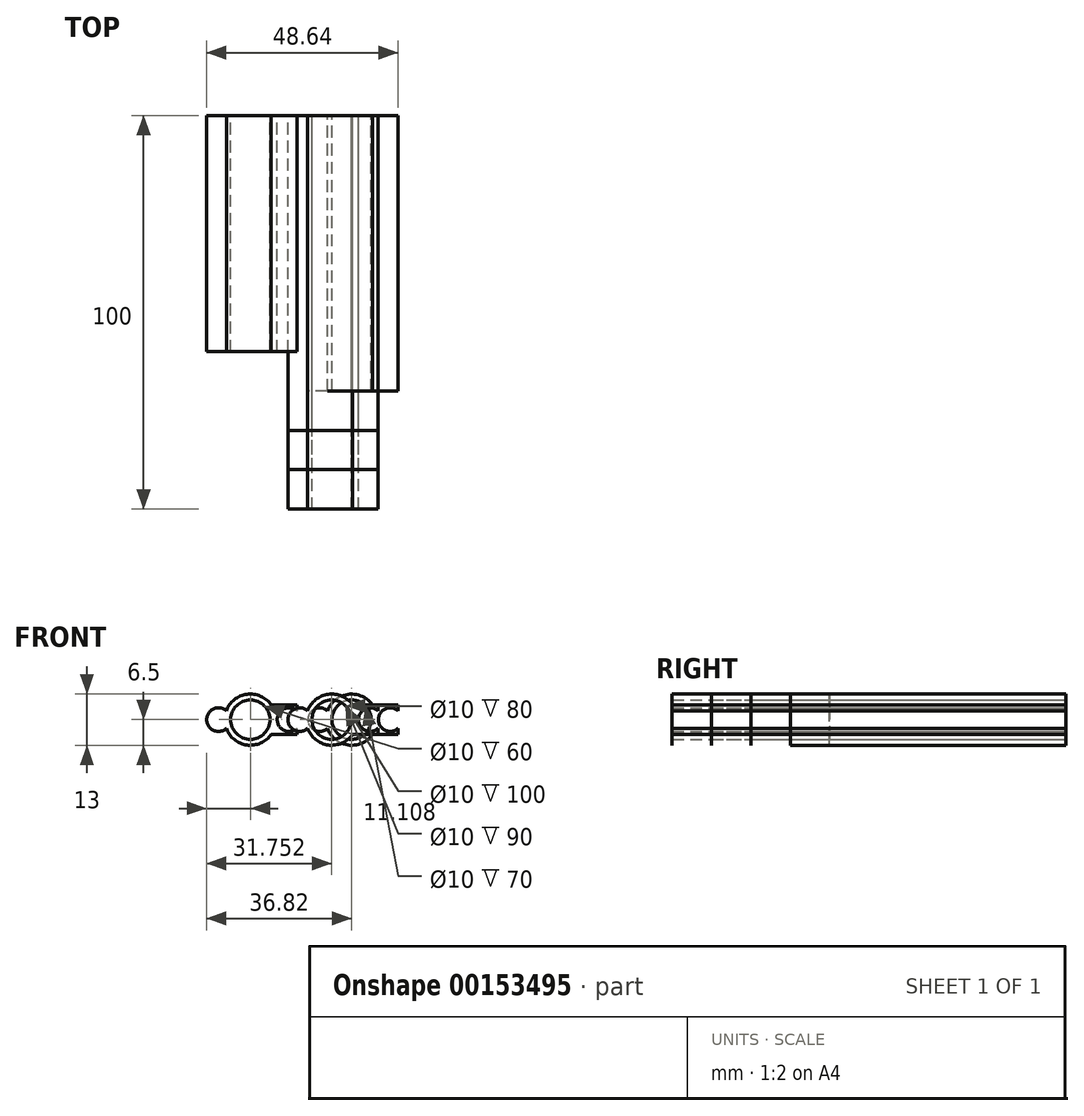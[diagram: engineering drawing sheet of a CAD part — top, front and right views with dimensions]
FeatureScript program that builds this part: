
annotation { "Feature Type Name" : "Feature", "Feature Type Description" : "" }
export const myFeature = defineFeature(function(context is Context, id is Id, definition is map)
    precondition{}
    {
        {
            var Q0;
            Q0=qCreatedBy(makeId("Front.planeOp"),FACE);
            var sketch = newSketch(context, id + "F0", { "sketchPlane" : qUnion([Q0])});
            skCircle(sketch, "E0", {"center": v(0, 0) * mm, "radius": 6.5 * mm});
            skArc(sketch, "E1", {"start": v(-6.1, 2.24) * mm, "mid": v(-11.1, 0) * mm, "end": v(-6.1, -2.24) * mm});
            skLineSegment(sketch, "E2", {"start": v(5.32, 3.74) * mm, "end": v(11.82, 3.74) * mm});
            skLineSegment(sketch, "E3", {"start": v(11.82, 3.74) * mm, "end": v(11.82, 2.24) * mm});
            skLineSegment(sketch, "E4", {"start": v(5.32, -3.74) * mm, "end": v(11.82, -3.74) * mm});
            skLineSegment(sketch, "E5", {"start": v(11.82, -3.74) * mm, "end": v(11.82, -2.24) * mm});
            skArc(sketch, "E6", {"start": v(11.82, 2.24) * mm, "mid": v(6.82, 0) * mm, "end": v(11.82, -2.24) * mm});
            skCircle(sketch, "E7", {"center": v(0, 0) * mm, "radius": 5 * mm});
            skSolve(sketch);
        }
        {
            var Q0;
            Q0=makeQuery(id+"F0.imprint","IMPRINT",FACE,{"disambiguationData":[TD([[makeQuery(id+"F0.imprint","IMPRINT",EDGE,{"derivedFrom":sQuery(id+"F0.wireOp",EDGE,"E7")}),-1.0]])]});
            var Q1;
            Q1=makeQuery(id+"F0.imprint","IMPRINT",FACE,{"disambiguationData":[TD([[makeQuery(id+"F0.imprint","IMPRINT",EDGE,{"derivedFrom":sQuery(id+"F0.wireOp",EDGE,"E1")}),1.0]])]});
            var Q2;
            {var subQ1=sQuery(id+"F0.wireOp",EDGE,"E2");Q2=makeQuery(id+"F0.imprint","IMPRINT",FACE,{"disambiguationData":[TD([[makeQuery(id+"F0.imprint","IMPRINT",EDGE,{"derivedFrom":subQ1}),-1.0]])]});}
            extrude(context, id + "F1", {"entities" : qUnion([Q0, Q1, Q2]), "depth" : 70 * mm});
        }
        {
            var Q0;
            Q0=qCreatedBy(makeId("Front.planeOp"),FACE);
            var sketch = newSketch(context, id + "F2", { "sketchPlane" : qUnion([Q0])});
            skCircle(sketch, "E8", {"center": v(-25.71, 0) * mm, "radius": 6.5 * mm});
            skArc(sketch, "E9", {"start": v(-31.82, 2.24) * mm, "mid": v(-36.61, -1.09) * mm, "end": v(-30.83, -0.3) * mm});
            skLineSegment(sketch, "E10", {"start": v(-20.4, 3.74) * mm, "end": v(-13.9, 3.74) * mm});
            skLineSegment(sketch, "E11", {"start": v(-13.9, 3.74) * mm, "end": v(-13.9, 2.24) * mm});
            skLineSegment(sketch, "E12", {"start": v(-20.4, -3.74) * mm, "end": v(-13.9, -3.74) * mm});
            skLineSegment(sketch, "E13", {"start": v(-13.9, -3.74) * mm, "end": v(-13.9, -2.24) * mm});
            skArc(sketch, "E14", {"start": v(-13.9, 2.24) * mm, "mid": v(-18.9, 0) * mm, "end": v(-13.9, -2.24) * mm});
            skCircle(sketch, "E15", {"center": v(-25.71, 0) * mm, "radius": 5 * mm});
            skSolve(sketch);
        }
        {
            var Q0;
            {var subQ0=sQuery(id+"F2.wireOp",EDGE,"E9");var subQ1=sQuery(id+"F2.wireOp",EDGE,"E8");var subQ2=makeQuery(id+"F2.imprint","INTERSECT",VERTEX,{"disambiguationData":[OD(0.0)],"derivedFrom":[subQ1,subQ0]});Q0=makeQuery(id+"F2.imprint","IMPRINT",FACE,{"disambiguationData":[TD([[makeQuery(id+"F2.imprint","IMPRINT",EDGE,{"disambiguationData":[TD([[subQ2,-1.0]])],"derivedFrom":subQ1}),-1.0]])]});}
            var Q1;
            Q1=makeQuery(id+"F2.imprint","IMPRINT",FACE,{"disambiguationData":[TD([[makeQuery(id+"F2.imprint","IMPRINT",EDGE,{"derivedFrom":sQuery(id+"F2.wireOp",EDGE,"E15")}),-1.0]])]});
            var Q2;
            {var subQ1=sQuery(id+"F2.wireOp",EDGE,"E10");Q2=makeQuery(id+"F2.imprint","IMPRINT",FACE,{"disambiguationData":[TD([[makeQuery(id+"F2.imprint","IMPRINT",EDGE,{"derivedFrom":subQ1}),-1.0]])]});}
            extrude(context, id + "F3", {"entities" : qUnion([Q0, Q1, Q2]), "depth" : 60 * mm});
        }
        {
            var Q0;
            Q0=qCreatedBy(makeId("Front.planeOp"),FACE);
            var sketch = newSketch(context, id + "F4", { "sketchPlane" : qUnion([Q0])});
            skCircle(sketch, "E16", {"center": v(-5.07, 0) * mm, "radius": 6.5 * mm});
            skArc(sketch, "E17", {"start": v(-11.17, 2.24) * mm, "mid": v(-16.17, 0) * mm, "end": v(-11.17, -2.24) * mm});
            skLineSegment(sketch, "E18", {"start": v(0.25, 3.74) * mm, "end": v(6.75, 3.74) * mm});
            skLineSegment(sketch, "E19", {"start": v(6.75, 3.74) * mm, "end": v(6.75, 2.24) * mm});
            skLineSegment(sketch, "E20", {"start": v(0.25, -3.74) * mm, "end": v(6.75, -3.74) * mm});
            skLineSegment(sketch, "E21", {"start": v(6.75, -3.74) * mm, "end": v(6.75, -2.24) * mm});
            skArc(sketch, "E22", {"start": v(6.75, 2.24) * mm, "mid": v(1.75, 0) * mm, "end": v(6.75, -2.24) * mm});
            skCircle(sketch, "E23", {"center": v(-5.07, 0) * mm, "radius": 5 * mm});
            skSolve(sketch);
        }
        {
            var Q0;
            {var subQ0=sQuery(id+"F4.wireOp",EDGE,"E17");Q0=makeQuery(id+"F4.imprint","IMPRINT",FACE,{"disambiguationData":[TD([[makeQuery(id+"F4.imprint","IMPRINT",EDGE,{"derivedFrom":subQ0}),1.0]])]});}
            var Q1;
            Q1=makeQuery(id+"F4.imprint","IMPRINT",FACE,{"disambiguationData":[TD([[makeQuery(id+"F4.imprint","IMPRINT",EDGE,{"derivedFrom":sQuery(id+"F4.wireOp",EDGE,"E23")}),-1.0]])]});
            var Q2;
            {var subQ1=sQuery(id+"F4.wireOp",EDGE,"E18");Q2=makeQuery(id+"F4.imprint","IMPRINT",FACE,{"disambiguationData":[TD([[makeQuery(id+"F4.imprint","IMPRINT",EDGE,{"derivedFrom":subQ1}),-1.0]])]});}
            extrude(context, id + "F5", {"entities" : qUnion([Q0, Q1, Q2]), "depth" : 80 * mm});
        }
        {
            var Q0;
            Q0=qCreatedBy(makeId("Front.planeOp"),FACE);
            var sketch = newSketch(context, id + "F6", { "sketchPlane" : qUnion([Q0])});
            skCircle(sketch, "E24", {"center": v(-5.07, 0) * mm, "radius": 6.5 * mm});
            skArc(sketch, "E25", {"start": v(-11.17, 2.24) * mm, "mid": v(-16.17, 0) * mm, "end": v(-11.17, -2.24) * mm});
            skLineSegment(sketch, "E26", {"start": v(0.25, 3.74) * mm, "end": v(6.75, 3.74) * mm});
            skLineSegment(sketch, "E27", {"start": v(6.75, 3.74) * mm, "end": v(6.75, 2.24) * mm});
            skLineSegment(sketch, "E28", {"start": v(0.25, -3.74) * mm, "end": v(6.75, -3.74) * mm});
            skLineSegment(sketch, "E29", {"start": v(6.75, -3.74) * mm, "end": v(6.75, -2.24) * mm});
            skArc(sketch, "E30", {"start": v(6.75, 2.24) * mm, "mid": v(1.75, 0) * mm, "end": v(6.75, -2.24) * mm});
            skCircle(sketch, "E31", {"center": v(-5.07, 0) * mm, "radius": 5 * mm});
            skSolve(sketch);
        }
        {
            var Q0;
            {var subQ0=sQuery(id+"F6.wireOp",EDGE,"E25");Q0=makeQuery(id+"F6.imprint","IMPRINT",FACE,{"disambiguationData":[TD([[makeQuery(id+"F6.imprint","IMPRINT",EDGE,{"derivedFrom":subQ0}),1.0]])]});}
            var Q1;
            Q1=makeQuery(id+"F6.imprint","IMPRINT",FACE,{"disambiguationData":[TD([[makeQuery(id+"F6.imprint","IMPRINT",EDGE,{"derivedFrom":sQuery(id+"F6.wireOp",EDGE,"E31")}),-1.0]])]});
            var Q2;
            {var subQ1=sQuery(id+"F6.wireOp",EDGE,"E26");Q2=makeQuery(id+"F6.imprint","IMPRINT",FACE,{"disambiguationData":[TD([[makeQuery(id+"F6.imprint","IMPRINT",EDGE,{"derivedFrom":subQ1}),-1.0]])]});}
            extrude(context, id + "F7", {"entities" : qUnion([Q0, Q1, Q2]), "depth" : 90 * mm});
        }
        {
            var Q0;
            Q0=qCreatedBy(makeId("Front.planeOp"),FACE);
            var sketch = newSketch(context, id + "F8", { "sketchPlane" : qUnion([Q0])});
            skCircle(sketch, "E32", {"center": v(-5.07, 0) * mm, "radius": 6.5 * mm});
            skArc(sketch, "E33", {"start": v(-11.17, 2.24) * mm, "mid": v(-16.17, 0) * mm, "end": v(-11.17, -2.24) * mm});
            skLineSegment(sketch, "E34", {"start": v(0.25, 3.74) * mm, "end": v(6.75, 3.74) * mm});
            skLineSegment(sketch, "E35", {"start": v(6.75, 3.74) * mm, "end": v(6.75, 2.24) * mm});
            skLineSegment(sketch, "E36", {"start": v(0.25, -3.74) * mm, "end": v(6.75, -3.74) * mm});
            skLineSegment(sketch, "E37", {"start": v(6.75, -3.74) * mm, "end": v(6.75, -2.24) * mm});
            skArc(sketch, "E38", {"start": v(6.75, 2.24) * mm, "mid": v(1.75, 0) * mm, "end": v(6.75, -2.24) * mm});
            skCircle(sketch, "E39", {"center": v(-5.07, 0) * mm, "radius": 5 * mm});
            skSolve(sketch);
        }
        {
            var Q0;
            {var subQ0=sQuery(id+"F8.wireOp",EDGE,"E33");Q0=makeQuery(id+"F8.imprint","IMPRINT",FACE,{"disambiguationData":[TD([[makeQuery(id+"F8.imprint","IMPRINT",EDGE,{"derivedFrom":subQ0}),1.0]])]});}
            var Q1;
            Q1=makeQuery(id+"F8.imprint","IMPRINT",FACE,{"disambiguationData":[TD([[makeQuery(id+"F8.imprint","IMPRINT",EDGE,{"derivedFrom":sQuery(id+"F8.wireOp",EDGE,"E39")}),-1.0]])]});
            var Q2;
            {var subQ1=sQuery(id+"F8.wireOp",EDGE,"E34");Q2=makeQuery(id+"F8.imprint","IMPRINT",FACE,{"disambiguationData":[TD([[makeQuery(id+"F8.imprint","IMPRINT",EDGE,{"derivedFrom":subQ1}),-1.0]])]});}
            extrude(context, id + "F9", {"entities" : qUnion([Q0, Q1, Q2]), "depth" : 100 * mm});
        }
    });
